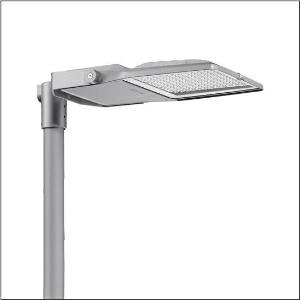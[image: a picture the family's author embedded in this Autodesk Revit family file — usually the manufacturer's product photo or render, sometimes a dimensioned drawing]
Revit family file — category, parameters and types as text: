
# Revit family: floodlight_fl_21_iq_midi___pl43_5xa7781f2a3a_7a49
name_source: partatom
category: Lighting Fixtures
units: mm (PartAtom-declared; Revit-internal decimal feet)

## family parameters
Cut with Voids When Loaded = No
Host = Face
Light Source = No
Part Type = Normal
Room Calculation Point = No
Round Connector Dimension = Use Diameter
Shared = No

## types (1)
- --- (1 x LED, 36680 lm, 270.2 W, 3000K)
    Apparent Load = 270 VA
    CIE Flux Codes = 27 78 99 100 100
    Color Rendering = 70
    Color Temperature = 3000K
    Default Elevation = 1800 mm
    Description = Floodlight FL 21 iQ midi, floodlight, primary light control with lens, of PMMA, primary optical cover: protective disc, of toughened safety glass, transparent, light distribution: PL43, light emission: direct distribution, installation type: surface-mounted, LED, High Power LED, rated luminous flux: 36.680lm, luminous efficacy: 136lm/W, light colour: 730, colour temperature: 3000K, control gear: ECG iQ, control: optimised constant luminous flux control (CLO 2.0), Desk-Remote (wireless, voltage-free reading and setting of iQ features in the workshop via application-optimized NFC function/RFID function), Light-Fading, Smart-Wire, Night-Set, Lumen-Switch, Temp-Guard, Auto-Match, with terminal, 6-pole, mains connection: 220..240V, AC, 50/60Hz, start of lifetime: 270W, end of service life: 287W, reduction: 117W, luminaire housing, of diecast aluminium, powder-coated, Siteco® metallic grey (DB 702S), corrosivity category C5 mid according to DIN EN ISO 12944, sealing non-destructively replaceable, please order mast flange separately, mast bracket, of steel, galvanised, powder-coated, Siteco® metallic grey (DB 702S), protection rating (complete): IP66, insulation class (complete): insulation class II (safety insulation), certification: CE, protection symbol: D, impact resistance: IK08, permissible operating ambient temperature: -40..+40°C, permissible operating ambient temperature for outdoor applications: -40..+50°C, standard: DIN EN 12944, LABS conformity tested according to VDMA 24364:2018-05, packaging unit: 1 piece

Light Distribution: PL43
    Height = 76 mm
    Lamp = 1 x LED
    Lamp Light Flux = 36680 lm
    Lamp Power = 270.2 W
    Lamp count = 1
    Length = 657 mm
    Luminous efficacy = 136 lm/W
    Manufacturer = Siteco
    ModVariant = No
    Model = 5XA7781F2A3A
    Number of Poles = 1
    OnlyDefault = Yes
    Power Factor = 1
    Product Name = Floodlight FL 21 iQ midi | PL43
    Product group = floodlight | pylon annexe
    ProductGroupID = 6200
    Protection Class = Protection class II
    Protection Degree = IP 66
    RLX_Detail_Level = 1
    RLX_Emergency_Light_Flux = 0 lm
    RLX_Emergency_Type = 0
    RLX_Emergency_Type_DB = No
    RlxData = <blob elided: 153453 chars, md5=02651ac8>
    Socket = socket
    Standby Power = 0 W
    System Light Flux = 36680 lm
    System Power = 270 W
    Type Comments = factory setting: luminous flux: 100 % | dim-lin: 254 | 620 mA
    Type Image = l_1007123.jpg
    URL = http://relux.com
    VarID = @adj_035015
    Voltage = 0 V
    Weight = 0.00 kg
    Width = 442 mm

## geometry (parser evidence)
native form markers: Blend x4, Sweep x13
no freeform markers — native parametric forms only
